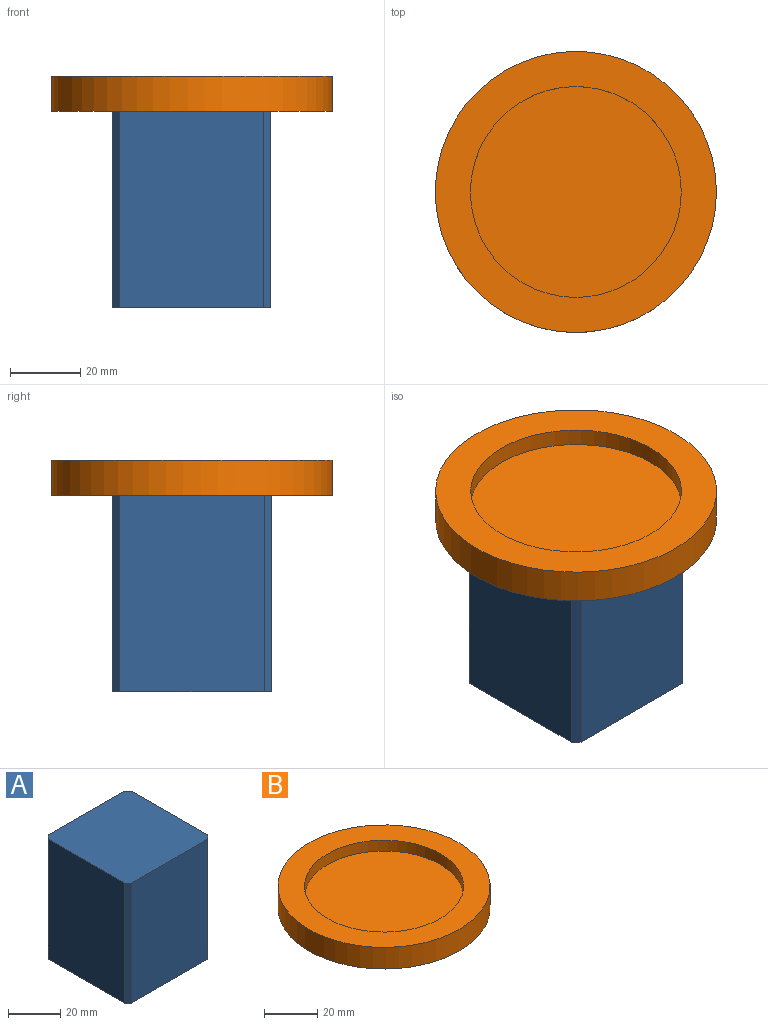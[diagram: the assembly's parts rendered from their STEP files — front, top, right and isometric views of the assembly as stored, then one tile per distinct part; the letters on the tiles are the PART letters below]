
ASSEMBLY  parts=2 mates=1
PART A: 10 faces, bbox 45x45x56 mm
  f0: plane 56x41mm, normal (1,0,0), area 2296mm2, adj f4,f5,f7,f8
  f1: plane 56x41mm, normal (0,1,0), area 2296mm2, adj f4,f5,f8,f9
  f2: plane 56x41mm, normal (-1,0,0), area 2296mm2, adj f4,f5,f6,f9
  f3: plane 56x41mm, normal (0,-1,0), area 2296mm2, adj f4,f5,f6,f7
  f4: plane 45x45mm, normal (0,0,-1), area 2017mm2, adj f0,f1,f2,f3,f6,f7,f8,f9
  f5: plane 45x45mm, normal (0,0,1), area 2017mm2, adj f0,f1,f2,f3,f6,f7,f8,f9
  f6: plane 56x2mm, normal (-0.71,-0.71,0), area 158.4mm2, adj f2,f3,f4,f5
  f7: plane 56x2mm, normal (0.71,-0.71,0), area 158.4mm2, adj f0,f3,f4,f5
  f8: plane 56x2mm, normal (0.71,0.71,0), area 158.4mm2, adj f0,f1,f4,f5
  f9: plane 56x2mm, normal (-0.71,0.71,0), area 158.4mm2, adj f1,f2,f4,f5
PART B: 5 faces, bbox 80x80x10 mm
  f0: cylinder r=40mm len=80mm, axis (0,0,-1), area 2513.3mm2, adj f1,f2
  f1: plane 80x80mm, normal (0,0,1), area 2199.1mm2, adj f0,f3
  f2: plane 80x80mm, normal (0,0,-1), area 5026.5mm2, adj f0
  f3: cylinder r=30mm len=60mm, axis (0,0,1), area 942.5mm2, adj f1,f4
  f4: plane 60x60mm, normal (0,0,1), area 2827.4mm2, adj f3
PLACE A at identity fixed
PLACE B t=(0,0,4)mm
MATE fastened B.f0 <-> A.f5  axis (0,0,-1) through (0,0,4)mm
